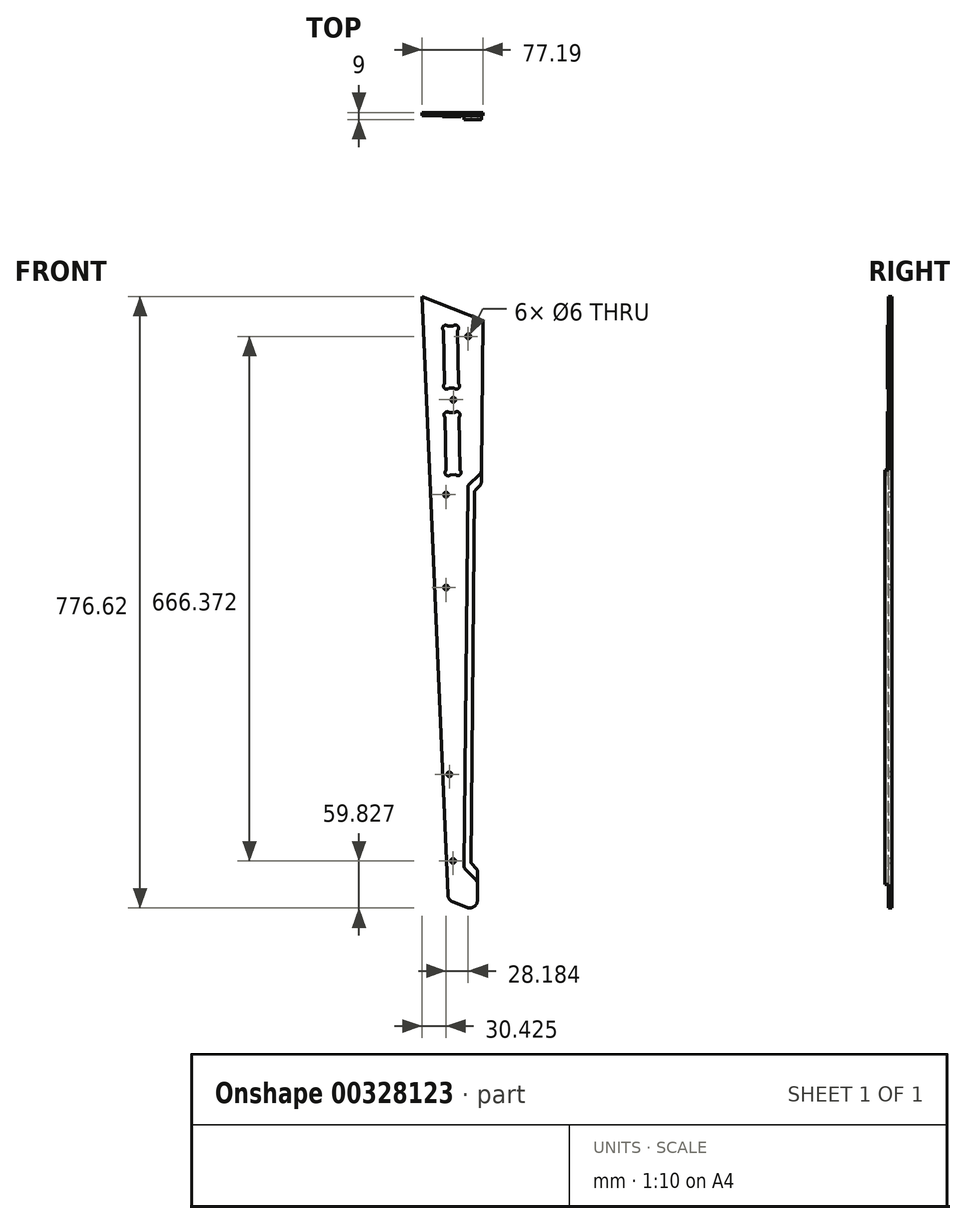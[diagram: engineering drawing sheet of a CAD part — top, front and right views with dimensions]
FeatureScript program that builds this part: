
annotation { "Feature Type Name" : "Feature", "Feature Type Description" : "" }
export const myFeature = defineFeature(function(context is Context, id is Id, definition is map)
    precondition{}
    {
        {
            var Q0;
            Q0=qCreatedBy(makeId("Front.planeOp"),FACE);
            var sketch = newSketch(context, id + "F0", { "sketchPlane" : qUnion([Q0])});
            skArc(sketch, "E0", {"start": v(-55.36, -345.94) * mm, "mid": v(-46.11, -344.91) * mm, "end": v(-41.72, -336.72) * mm});
            skLineSegment(sketch, "E1", {"start": v(-41.72, -336.72) * mm, "end": v(-34.9, 399.8) * mm});
            skLineSegment(sketch, "E2", {"start": v(-34.9, 399.8) * mm, "end": v(-112.09, 429.99) * mm});
            skLineSegment(sketch, "E3", {"start": v(-112.09, 429.99) * mm, "end": v(-79.3, -330.18) * mm});
            skArc(sketch, "E4", {"start": v(-79.3, -330.18) * mm, "mid": v(-77.45, -335.56) * mm, "end": v(-72.95, -339.06) * mm});
            skLineSegment(sketch, "E5", {"start": v(-72.95, -339.06) * mm, "end": v(-55.36, -345.94) * mm});
            skCircle(sketch, "E6", {"center": v(-81.67, 178.45) * mm, "radius": 3 * mm});
            skCircle(sketch, "E7", {"center": v(-81.55, 60.4) * mm, "radius": 3 * mm});
            skCircle(sketch, "E8", {"center": v(-53.48, 379.57) * mm, "radius": 3 * mm});
            skCircle(sketch, "E9", {"center": v(-72.34, 298.97) * mm, "radius": 3 * mm});
            skCircle(sketch, "E10", {"center": v(-72.76, -286.8) * mm, "radius": 3 * mm});
            skCircle(sketch, "E11", {"center": v(-77.5, -176.9) * mm, "radius": 3 * mm});
            skArc(sketch, "E12", {"start": v(-83.71, 319.13) * mm, "mid": v(-83.62, 313.47) * mm, "end": v(-77.96, 313.57) * mm});
            skLineSegment(sketch, "E13", {"start": v(-77.96, 313.57) * mm, "end": v(-71.27, 313.68) * mm});
            skArc(sketch, "E14", {"start": v(-71.27, 313.68) * mm, "mid": v(-65.62, 313.78) * mm, "end": v(-65.71, 319.43) * mm});
            skLineSegment(sketch, "E15", {"start": v(-65.71, 319.43) * mm, "end": v(-66.86, 387.1) * mm});
            skArc(sketch, "E16", {"start": v(-66.86, 387.1) * mm, "mid": v(-66.96, 392.76) * mm, "end": v(-72.61, 392.67) * mm});
            skLineSegment(sketch, "E17", {"start": v(-72.61, 392.67) * mm, "end": v(-79.3, 392.56) * mm});
            skArc(sketch, "E18", {"start": v(-79.3, 392.56) * mm, "mid": v(-84.95, 392.46) * mm, "end": v(-84.86, 386.8) * mm});
            skLineSegment(sketch, "E19", {"start": v(-84.86, 386.8) * mm, "end": v(-83.71, 319.13) * mm});
            skLineSegment(sketch, "E20", {"start": v(-69.41, 203.7) * mm, "end": v(-76.1, 203.58) * mm});
            skArc(sketch, "E21", {"start": v(-76.1, 203.58) * mm, "mid": v(-81.75, 203.49) * mm, "end": v(-81.85, 209.14) * mm});
            skLineSegment(sketch, "E22", {"start": v(-81.85, 209.14) * mm, "end": v(-83, 276.82) * mm});
            skArc(sketch, "E23", {"start": v(-83, 276.82) * mm, "mid": v(-83.1, 282.48) * mm, "end": v(-77.44, 282.57) * mm});
            skLineSegment(sketch, "E24", {"start": v(-77.44, 282.57) * mm, "end": v(-70.75, 282.69) * mm});
            skArc(sketch, "E25", {"start": v(-70.75, 282.69) * mm, "mid": v(-65.1, 282.78) * mm, "end": v(-65, 277.13) * mm});
            skLineSegment(sketch, "E26", {"start": v(-65, 277.13) * mm, "end": v(-63.85, 209.45) * mm});
            skArc(sketch, "E27", {"start": v(-63.85, 209.45) * mm, "mid": v(-63.76, 203.8) * mm, "end": v(-69.41, 203.7) * mm});
            skArc(sketch, "E28", {"start": v(-32, -319.55) * mm, "mid": v(-36.82, -324.29) * mm, "end": v(-41.56, -319.46) * mm});
            skLineSegment(sketch, "E29", {"start": v(-41.56, -319.46) * mm, "end": v(-41.53, -316.78) * mm});
            skArc(sketch, "E30", {"start": v(-41.53, -316.78) * mm, "mid": v(-42.11, -313.71) * mm, "end": v(-43.82, -311.1) * mm});
            skLineSegment(sketch, "E31", {"start": v(-43.82, -311.1) * mm, "end": v(-57.4, -297.27) * mm});
            skArc(sketch, "E32", {"start": v(-57.4, -297.27) * mm, "mid": v(-58.25, -295.97) * mm, "end": v(-58.54, -294.44) * mm});
            skLineSegment(sketch, "E33", {"start": v(-58.54, -294.44) * mm, "end": v(-54.07, 187.8) * mm});
            skArc(sketch, "E34", {"start": v(-54.07, 187.8) * mm, "mid": v(-53.76, 189.33) * mm, "end": v(-52.88, 190.62) * mm});
            skLineSegment(sketch, "E35", {"start": v(-52.88, 190.62) * mm, "end": v(-39.05, 204.2) * mm});
            skArc(sketch, "E36", {"start": v(-39.05, 204.2) * mm, "mid": v(-37.3, 206.77) * mm, "end": v(-36.66, 209.83) * mm});
            skLineSegment(sketch, "E37", {"start": v(-36.66, 209.83) * mm, "end": v(-36.63, 212.51) * mm});
            skArc(sketch, "E38", {"start": v(-36.63, 212.51) * mm, "mid": v(-31.8, 217.25) * mm, "end": v(-27.07, 212.42) * mm});
            skLineSegment(sketch, "E39", {"start": v(-27.07, 212.42) * mm, "end": v(-32, -319.55) * mm});
            skArc(sketch, "E40", {"start": v(-43.68, -296.1) * mm, "mid": v(-41.97, -298.71) * mm, "end": v(-41.4, -301.78) * mm});
            skLineSegment(sketch, "E41", {"start": v(-41.4, -301.78) * mm, "end": v(-41.42, -304.47) * mm});
            skArc(sketch, "E42", {"start": v(-41.42, -304.47) * mm, "mid": v(-36.68, -309.3) * mm, "end": v(-31.85, -304.55) * mm});
            skLineSegment(sketch, "E43", {"start": v(-31.85, -304.55) * mm, "end": v(-27.2, 197.42) * mm});
            skArc(sketch, "E44", {"start": v(-27.2, 197.42) * mm, "mid": v(-31.94, 202.25) * mm, "end": v(-36.77, 197.51) * mm});
            skLineSegment(sketch, "E45", {"start": v(-36.77, 197.51) * mm, "end": v(-36.8, 194.83) * mm});
            skArc(sketch, "E46", {"start": v(-36.8, 194.83) * mm, "mid": v(-37.43, 191.77) * mm, "end": v(-39.19, 189.2) * mm});
            skLineSegment(sketch, "E47", {"start": v(-39.19, 189.2) * mm, "end": v(-44.33, 184.15) * mm});
            skArc(sketch, "E48", {"start": v(-44.33, 184.15) * mm, "mid": v(-45.2, 182.86) * mm, "end": v(-45.53, 181.33) * mm});
            skLineSegment(sketch, "E49", {"start": v(-45.53, 181.33) * mm, "end": v(-49.87, -288.12) * mm});
            skArc(sketch, "E50", {"start": v(-49.87, -288.12) * mm, "mid": v(-49.58, -289.66) * mm, "end": v(-48.73, -290.96) * mm});
            skLineSegment(sketch, "E51", {"start": v(-48.73, -290.96) * mm, "end": v(-43.68, -296.1) * mm});
            skSolve(sketch);
        }
        {
            var Q0;
            Q0=makeQuery(id+"F0.imprint","IMPRINT",FACE,{"disambiguationData":[TD([[makeQuery(id+"F0.imprint","IMPRINT",EDGE,{"derivedFrom":sQuery(id+"F0.wireOp",EDGE,"E10")}),-1.0]])]});
            var Q1;
            Q1=makeQuery(id+"F0.imprint","IMPRINT",FACE,{"disambiguationData":[TD([[makeQuery(id+"F0.imprint","IMPRINT",EDGE,{"derivedFrom":sQuery(id+"F0.wireOp",EDGE,"E11")}),-1.0]])]});
            var Q2;
            Q2=makeQuery(id+"F0.imprint","IMPRINT",FACE,{"disambiguationData":[TD([[makeQuery(id+"F0.imprint","IMPRINT",EDGE,{"derivedFrom":sQuery(id+"F0.wireOp",EDGE,"E7")}),-1.0]])]});
            var Q3;
            Q3=makeQuery(id+"F0.imprint","IMPRINT",FACE,{"disambiguationData":[TD([[makeQuery(id+"F0.imprint","IMPRINT",EDGE,{"derivedFrom":sQuery(id+"F0.wireOp",EDGE,"E6")}),-1.0]])]});
            var Q4;
            {var subQ2=sQuery(id+"F0.wireOp",EDGE,"E0");Q4=makeQuery(id+"F0.imprint","IMPRINT",FACE,{"disambiguationData":[TD([[makeQuery(id+"F0.imprint","IMPRINT",EDGE,{"derivedFrom":subQ2}),1.0]])]});}
            var Q5;
            Q5=makeQuery(id+"F0.imprint","IMPRINT",FACE,{"disambiguationData":[TD([[makeQuery(id+"F0.imprint","IMPRINT",EDGE,{"derivedFrom":sQuery(id+"F0.wireOp",EDGE,"E8")}),-1.0]])]});
            var Q6;
            Q6=makeQuery(id+"F0.imprint","IMPRINT",FACE,{"disambiguationData":[TD([[makeQuery(id+"F0.imprint","IMPRINT",EDGE,{"derivedFrom":sQuery(id+"F0.wireOp",EDGE,"E9")}),-1.0]])]});
            var Q7;
            {var subQ3=sQuery(id+"F0.wireOp",EDGE,"E30");Q7=makeQuery(id+"F0.imprint","IMPRINT",FACE,{"disambiguationData":[TD([[makeQuery(id+"F0.imprint","IMPRINT",EDGE,{"derivedFrom":subQ3}),-1.0]])]});}
            var Q8;
            {var subQ1=sQuery(id+"F0.wireOp",EDGE,"E40");Q8=makeQuery(id+"F0.imprint","IMPRINT",FACE,{"disambiguationData":[TD([[makeQuery(id+"F0.imprint","IMPRINT",EDGE,{"derivedFrom":subQ1}),1.0]])]});}
            var Q9;
            Q9=makeQuery(id+"F0.imprint","IMPRINT",FACE,{"disambiguationData":[TD([[makeQuery(id+"F0.imprint","IMPRINT",EDGE,{"derivedFrom":sQuery(id+"F0.wireOp",EDGE,"E20")}),-1.0]])]});
            var Q10;
            Q10=makeQuery(id+"F0.imprint","IMPRINT",FACE,{"disambiguationData":[TD([[makeQuery(id+"F0.imprint","IMPRINT",EDGE,{"derivedFrom":sQuery(id+"F0.wireOp",EDGE,"E12")}),1.0]])]});
            extrude(context, id + "F1", {"entities" : qUnion([Q0, Q1, Q2, Q3, Q4, Q5, Q6, Q7, Q8, Q9, Q10]), "oppositeDirection" : true, "depth" : 18 * mm});
        }
        {
            var Q0;
            Q0=makeQuery(id+"F0.imprint","IMPRINT",FACE,{"disambiguationData":[TD([[makeQuery(id+"F0.imprint","IMPRINT",EDGE,{"derivedFrom":sQuery(id+"F0.wireOp",EDGE,"E10")}),-1.0]])]});
            var Q1;
            Q1=makeQuery(id+"F0.imprint","IMPRINT",FACE,{"disambiguationData":[TD([[makeQuery(id+"F0.imprint","IMPRINT",EDGE,{"derivedFrom":sQuery(id+"F0.wireOp",EDGE,"E11")}),-1.0]])]});
            var Q2;
            Q2=makeQuery(id+"F0.imprint","IMPRINT",FACE,{"disambiguationData":[TD([[makeQuery(id+"F0.imprint","IMPRINT",EDGE,{"derivedFrom":sQuery(id+"F0.wireOp",EDGE,"E7")}),-1.0]])]});
            var Q3;
            Q3=makeQuery(id+"F0.imprint","IMPRINT",FACE,{"disambiguationData":[TD([[makeQuery(id+"F0.imprint","IMPRINT",EDGE,{"derivedFrom":sQuery(id+"F0.wireOp",EDGE,"E6")}),-1.0]])]});
            var Q4;
            Q4=makeQuery(id+"F0.imprint","IMPRINT",FACE,{"disambiguationData":[TD([[makeQuery(id+"F0.imprint","IMPRINT",EDGE,{"derivedFrom":sQuery(id+"F0.wireOp",EDGE,"E9")}),-1.0]])]});
            var Q5;
            Q5=makeQuery(id+"F0.imprint","IMPRINT",FACE,{"disambiguationData":[TD([[makeQuery(id+"F0.imprint","IMPRINT",EDGE,{"derivedFrom":sQuery(id+"F0.wireOp",EDGE,"E8")}),-1.0]])]});
            extrude(context, id + "F2", {"entities" : qUnion([Q0, Q1, Q2, Q3, Q4, Q5]), "operationType" : NewBodyOperationType.REMOVE, "oppositeDirection" : true, "depth" : 14 * mm});
        }
        {
            var Q0;
            {var subQ1=sQuery(id+"F0.wireOp",EDGE,"E40");Q0=makeQuery(id+"F0.imprint","IMPRINT",FACE,{"disambiguationData":[TD([[makeQuery(id+"F0.imprint","IMPRINT",EDGE,{"derivedFrom":subQ1}),1.0]])]});}
            extrude(context, id + "F3", {"entities" : qUnion([Q0]), "operationType" : NewBodyOperationType.REMOVE, "oppositeDirection" : true, "depth" : 9 * mm});
        }
        {
            var Q0;
            {var subQ3=sQuery(id+"F0.wireOp",EDGE,"E30");Q0=makeQuery(id+"F0.imprint","IMPRINT",FACE,{"disambiguationData":[TD([[makeQuery(id+"F0.imprint","IMPRINT",EDGE,{"derivedFrom":subQ3}),-1.0]])]});}
            extrude(context, id + "F4", {"entities" : qUnion([Q0]), "operationType" : NewBodyOperationType.REMOVE, "oppositeDirection" : true, "depth" : 6 * mm});
        }
        {
            var Q0;
            Q0=makeQuery(id+"F0.imprint","IMPRINT",FACE,{"disambiguationData":[TD([[makeQuery(id+"F0.imprint","IMPRINT",EDGE,{"derivedFrom":sQuery(id+"F0.wireOp",EDGE,"E20")}),-1.0]])]});
            var Q1;
            Q1=makeQuery(id+"F0.imprint","IMPRINT",FACE,{"disambiguationData":[TD([[makeQuery(id+"F0.imprint","IMPRINT",EDGE,{"derivedFrom":sQuery(id+"F0.wireOp",EDGE,"E12")}),1.0]])]});
            extrude(context, id + "F5", {"entities" : qUnion([Q0, Q1]), "operationType" : NewBodyOperationType.REMOVE, "oppositeDirection" : true, "depth" : 12.5 * mm});
        }
    });
